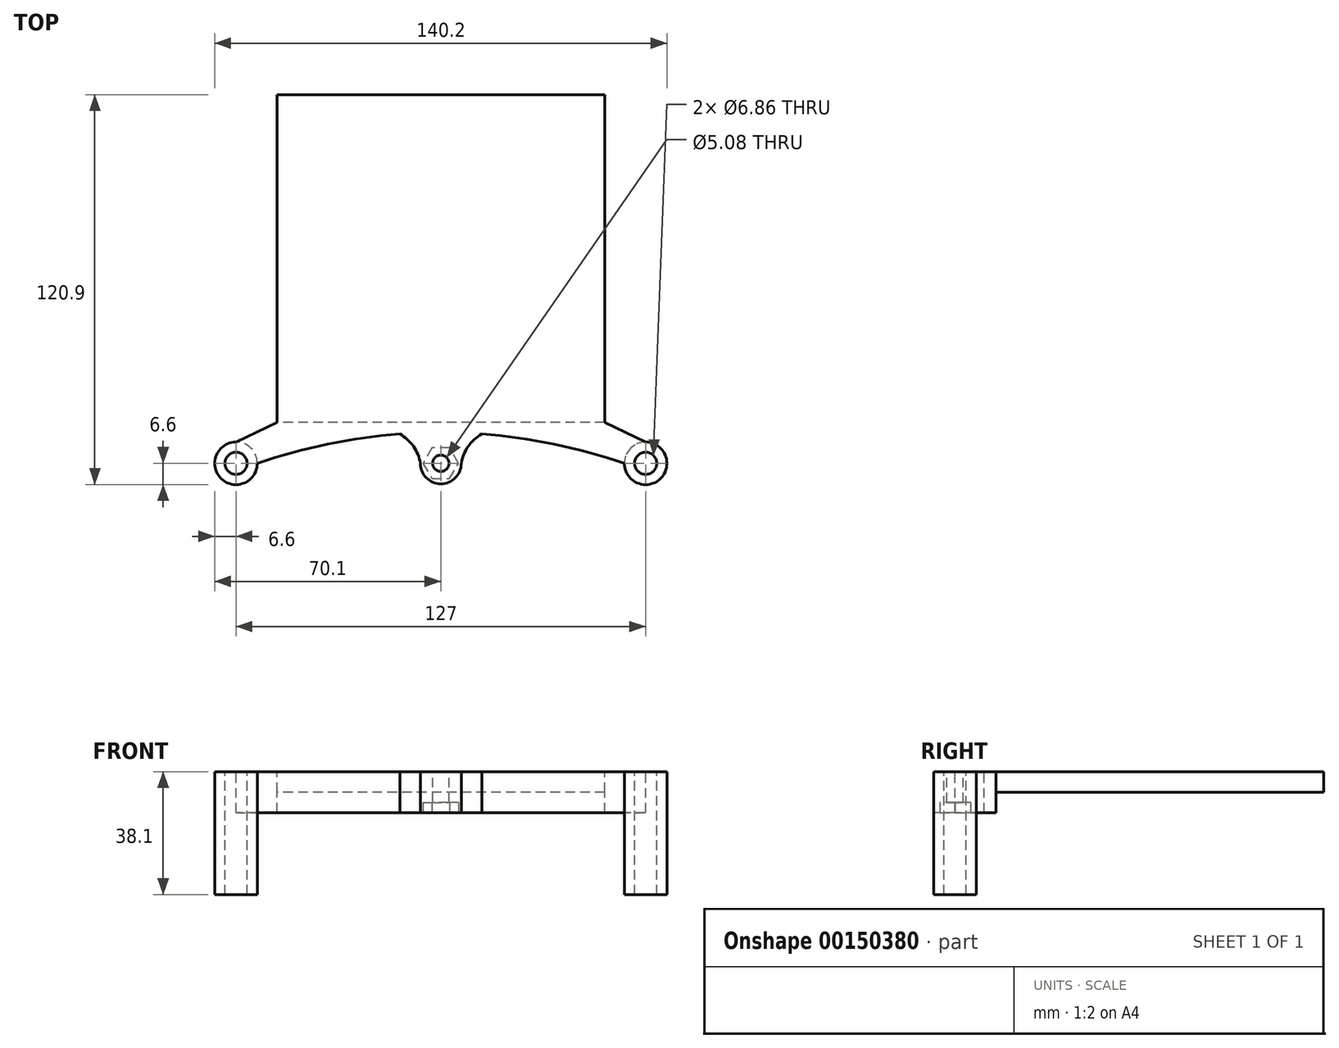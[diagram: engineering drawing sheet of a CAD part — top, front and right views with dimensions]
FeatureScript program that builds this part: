
annotation { "Feature Type Name" : "Feature", "Feature Type Description" : "" }
export const myFeature = defineFeature(function(context is Context, id is Id, definition is map)
    precondition{}
    {
        {
            var Q0;
            Q0=qCreatedBy(makeId("Top.planeOp"),FACE);
            var sketch = newSketch(context, id + "F0", { "sketchPlane" : qUnion([Q0])});
            skLineSegment(sketch, "E0.bottom", {"start": v(50.8, 50.8) * mm, "end": v(-50.8, 50.8) * mm});
            skLineSegment(sketch, "E0.top", {"start": v(50.8, -50.8) * mm, "end": v(-50.8, -50.8) * mm});
            skLineSegment(sketch, "E0.left", {"start": v(50.8, 50.8) * mm, "end": v(50.8, -50.8) * mm});
            skLineSegment(sketch, "E0.right", {"start": v(-50.8, 50.8) * mm, "end": v(-50.8, -50.8) * mm});
            skPoint(sketch, "E0.middle", {"position": v(0, 0) * mm});
            skSolve(sketch);
        }
        {
            var Q0;
            Q0 = qSketchRegion(id + "F0", true);
            extrude(context, id + "F1", {"entities" : qUnion([Q0]), "oppositeDirection" : true, "depth" : 6.35 * mm});
        }
        {
            var Q0;
            Q0=makeQuery(id+"F1.opExtrude","CAP_FACE",FACE,{"disambiguationData":[OSD([sQuery(id+"F0.wireOp",EDGE,"E0.bottom"),sQuery(id+"F0.wireOp",EDGE,"E0.top"),sQuery(id+"F0.wireOp",EDGE,"E0.left"),sQuery(id+"F0.wireOp",EDGE,"E0.right")])],"isStart":true});
            var sketch = newSketch(context, id + "F2", { "sketchPlane" : qUnion([Q0])});
            skCircle(sketch, "E1", {"center": v(-63.5, -63.5) * mm, "radius": 3.43 * mm});
            skCircle(sketch, "E2", {"center": v(63.5, -63.5) * mm, "radius": 3.43 * mm});
            skLineSegment(sketch, "E3", {"start": v(-63.5, -63.5) * mm, "end": v(0, -50.8) * mm, "construction": true});
            skLineSegment(sketch, "E4", {"start": v(0, -50.8) * mm, "end": v(63.5, -63.5) * mm, "construction": true});
            skLineSegment(sketch, "E5", {"start": v(-63.5, -63.5) * mm, "end": v(63.5, -63.5) * mm, "construction": true});
            skArc(sketch, "E6", {"start": v(-63.5, -56.9) * mm, "mid": v(-68.17, -68.17) * mm, "end": v(-56.9, -63.5) * mm});
            skArc(sketch, "E7", {"start": v(56.9, -63.5) * mm, "mid": v(68.17, -68.17) * mm, "end": v(63.5, -56.9) * mm});
            skLineSegment(sketch, "E8", {"start": v(-63.5, -56.9) * mm, "end": v(-50.8, -50.8) * mm});
            skLineSegment(sketch, "E9", {"start": v(-63.5, -63.5) * mm, "end": v(-63.5, -56.9) * mm, "construction": true});
            skArc(sketch, "E10", {"start": v(56.9, -63.5) * mm, "mid": v(35.1, -57.54) * mm, "end": v(12.7, -54.44) * mm});
            skLineSegment(sketch, "E11", {"start": v(50.8, -50.8) * mm, "end": v(63.5, -56.9) * mm});
            skLineSegment(sketch, "E12", {"start": v(63.5, -56.9) * mm, "end": v(63.5, -63.5) * mm, "construction": true});
            skCircle(sketch, "E13", {"center": v(0, -63.5) * mm, "radius": 6.35 * mm});
            skArc(sketch, "E14", {"start": v(-6.35, -63.5) * mm, "mid": v(-8.49, -58.24) * mm, "end": v(-12.7, -54.44) * mm});
            skArc(sketch, "E15", {"start": v(12.7, -54.44) * mm, "mid": v(8.49, -58.24) * mm, "end": v(6.35, -63.5) * mm});
            skCircle(sketch, "E16", {"center": v(0, -63.5) * mm, "radius": 2.54 * mm});
            skLineSegment(sketch, "E17", {"start": v(-12.7, -54.44) * mm, "end": v(0, -63.5) * mm, "construction": true});
            skLineSegment(sketch, "E18", {"start": v(12.7, -54.44) * mm, "end": v(0, -63.5) * mm, "construction": true});
            skLineSegment(sketch, "E19", {"start": v(-12.7, -54.44) * mm, "end": v(12.7, -54.44) * mm, "construction": true});
            skArc(sketch, "E20.trimOffspring", {"start": v(-12.7, -54.44) * mm, "mid": v(-35.1, -57.54) * mm, "end": v(-56.9, -63.5) * mm});
            skSolve(sketch);
        }
        {
            var Q0;
            Q0=makeQuery(id+"F2.imprint","IMPRINT",FACE,{"disambiguationData":[TD([[makeQuery(id+"F2.imprint","IMPRINT",EDGE,{"derivedFrom":sQuery(id+"F2.wireOp",EDGE,"E1")}),-1.0]])]});
            var Q1;
            Q1=makeQuery(id+"F2.imprint","IMPRINT",FACE,{"disambiguationData":[TD([[makeQuery(id+"F2.imprint","IMPRINT",EDGE,{"derivedFrom":sQuery(id+"F2.wireOp",EDGE,"E16")}),-1.0]])]});
            extrude(context, id + "F3", {"entities" : qUnion([Q0, Q1]), "operationType" : NewBodyOperationType.ADD, "oppositeDirection" : true, "depth" : 12.7 * mm});
        }
        {
            var Q0;
            Q0=makeQuery(id+"F3.opExtrude","CAP_FACE",FACE,{"disambiguationData":[OSD([sQuery(id+"F0.wireOp",EDGE,"E0.top"),sQuery(id+"F2.wireOp",EDGE,"E1"),sQuery(id+"F2.wireOp",EDGE,"E2"),sQuery(id+"F2.wireOp",EDGE,"E6"),sQuery(id+"F2.wireOp",EDGE,"E7"),sQuery(id+"F2.wireOp",EDGE,"E8"),sQuery(id+"F2.wireOp",EDGE,"E10"),sQuery(id+"F2.wireOp",EDGE,"E11"),sQuery(id+"F2.wireOp",EDGE,"E13"),sQuery(id+"F2.wireOp",EDGE,"E14"),sQuery(id+"F2.wireOp",EDGE,"E15"),sQuery(id+"F2.wireOp",EDGE,"E16"),sQuery(id+"F2.wireOp",EDGE,"E20.trimOffspring")])],"isStart":false});
            var sketch = newSketch(context, id + "F4", { "sketchPlane" : qUnion([Q0])});
            skCircle(sketch, "E21.0", {"center": v(-63.5, 63.5) * mm, "radius": 3.43 * mm});
            skArc(sketch, "E21.1", {"start": v(-63.5, 56.9) * mm, "mid": v(-68.17, 68.17) * mm, "end": v(-56.9, 63.5) * mm});
            skArc(sketch, "E22", {"start": v(-63.5, 56.9) * mm, "mid": v(-58.83, 58.83) * mm, "end": v(-56.9, 63.5) * mm});
            skArc(sketch, "E23.MirrorCS", {"start": v(63.5, 56.9) * mm, "mid": v(58.83, 58.83) * mm, "end": v(56.9, 63.5) * mm});
            skCircle(sketch, "E24.MirrorC", {"center": v(63.5, 63.5) * mm, "radius": 3.43 * mm});
            skArc(sketch, "E25.MirrorCS", {"start": v(63.5, 56.9) * mm, "mid": v(68.17, 68.17) * mm, "end": v(56.9, 63.5) * mm});
            skSolve(sketch);
        }
        {
            var Q0;
            Q0 = qSketchRegion(id + "F4", true);
            extrude(context, id + "F5", {"entities" : qUnion([Q0]), "operationType" : NewBodyOperationType.ADD, "depth" : 25.4 * mm});
        }
        {
            var Q0;
            Q0=makeQuery(id+"F3.opExtrude","CAP_FACE",FACE,{"disambiguationData":[OSD([sQuery(id+"F0.wireOp",EDGE,"E0.top"),sQuery(id+"F2.wireOp",EDGE,"E1"),sQuery(id+"F2.wireOp",EDGE,"E2"),sQuery(id+"F2.wireOp",EDGE,"E6"),sQuery(id+"F2.wireOp",EDGE,"E7"),sQuery(id+"F2.wireOp",EDGE,"E8"),sQuery(id+"F2.wireOp",EDGE,"E10"),sQuery(id+"F2.wireOp",EDGE,"E11"),sQuery(id+"F2.wireOp",EDGE,"E13"),sQuery(id+"F2.wireOp",EDGE,"E14"),sQuery(id+"F2.wireOp",EDGE,"E15"),sQuery(id+"F2.wireOp",EDGE,"E16"),sQuery(id+"F2.wireOp",EDGE,"E20.trimOffspring")])],"isStart":false});
            var sketch = newSketch(context, id + "F6", { "sketchPlane" : qUnion([Q0])});
            skCircle(sketch, "E26.cCircle", {"center": v(0, 63.5) * mm, "radius": 4.76 * mm, "construction": true});
            skLineSegment(sketch, "E26.0", {"start": v(-2.75, 68.26) * mm, "end": v(2.75, 68.26) * mm});
            skLineSegment(sketch, "E26.1", {"start": v(2.75, 68.26) * mm, "end": v(5.5, 63.5) * mm});
            skLineSegment(sketch, "E26.2", {"start": v(5.5, 63.5) * mm, "end": v(2.75, 58.74) * mm});
            skLineSegment(sketch, "E26.3", {"start": v(2.75, 58.74) * mm, "end": v(-2.75, 58.74) * mm});
            skLineSegment(sketch, "E26.4", {"start": v(-2.75, 58.74) * mm, "end": v(-5.5, 63.5) * mm});
            skLineSegment(sketch, "E26.5", {"start": v(-5.5, 63.5) * mm, "end": v(-2.75, 68.26) * mm});
            skPoint(sketch, "E26.0.midPoint", {"position": v(0, 68.26) * mm});
            skSolve(sketch);
        }
        {
            var Q0;
            Q0=makeQuery(id+"F6.imprint","IMPRINT",FACE,{"disambiguationData":[TD([[makeQuery(id+"F6.imprint","IMPRINT",EDGE,{"derivedFrom":sQuery(id+"F6.wireOp",EDGE,"E26.0")}),-1.0]])]});
            extrude(context, id + "F7", {"entities" : qUnion([Q0]), "operationType" : NewBodyOperationType.REMOVE, "oppositeDirection" : true, "depth" : 3.17 * mm});
        }
    });
